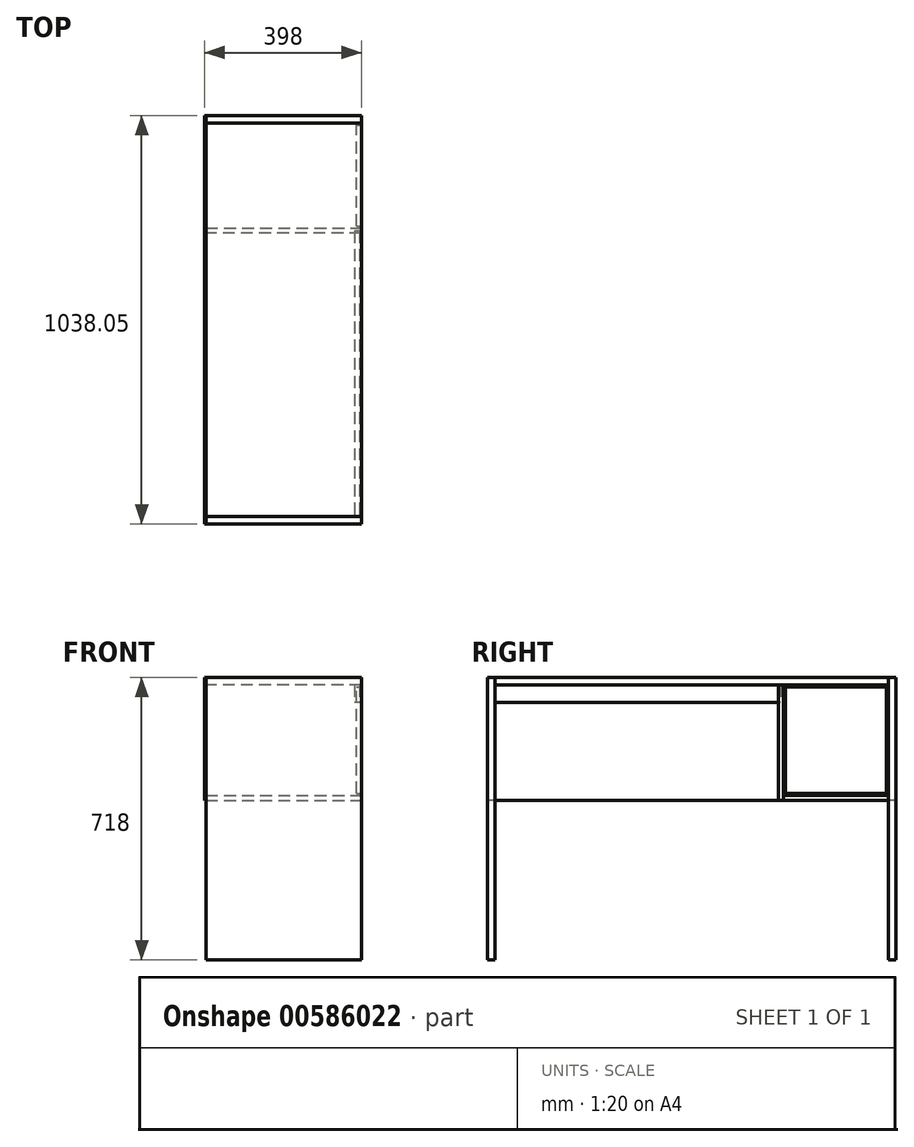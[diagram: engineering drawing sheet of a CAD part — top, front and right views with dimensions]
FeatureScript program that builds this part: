
annotation { "Feature Type Name" : "Feature", "Feature Type Description" : "" }
export const myFeature = defineFeature(function(context is Context, id is Id, definition is map)
    precondition{}
    {
        {
            var Q0;
            Q0=qCreatedBy(makeId("Front.planeOp"),FACE);
            var sketch = newSketch(context, id + "F0", { "sketchPlane" : qUnion([Q0])});
            skLineSegment(sketch, "E0.bottom", {"start": v(197.5, 359) * mm, "end": v(-197.5, 359) * mm});
            skLineSegment(sketch, "E0.top", {"start": v(197.5, -359) * mm, "end": v(-197.5, -359) * mm});
            skLineSegment(sketch, "E0.left", {"start": v(197.5, 359) * mm, "end": v(197.5, -359) * mm});
            skLineSegment(sketch, "E0.right", {"start": v(-197.5, 359) * mm, "end": v(-197.5, -359) * mm});
            skPoint(sketch, "E0.middle", {"position": v(0, 0) * mm});
            skSolve(sketch);
        }
        {
            var Q0;
            Q0 = qSketchRegion(id + "F0", true);
            extrude(context, id + "F1", {"entities" : qUnion([Q0]), "depth" : 19.05 * mm, "offsetDistance" : 25.4 * mm});
        }
        {
            var Q0;
            Q0=makeQuery(id+"F1.opExtrude","SWEPT_BODY",BODY,{"disambiguationData":[OSD([sQuery(id+"F0.wireOp",EDGE,"E0.bottom"),sQuery(id+"F0.wireOp",EDGE,"E0.top"),sQuery(id+"F0.wireOp",EDGE,"E0.left"),sQuery(id+"F0.wireOp",EDGE,"E0.right")])]});
            transform(context, id + "F2", {"entities" : qUnion([Q0]), "transformType" : TransformType.TRANSLATION_3D, "dx" : 0 * mm, "dy" : 1019 * mm, "dz" : 0 * mm, "makeCopy" : true});
        }
        {
            var Q0;
            Q0=makeQuery(id+"F1.opExtrude","SWEPT_FACE",FACE,{"disambiguationData":[OSD([sQuery(id+"F0.wireOp",EDGE,"E0.bottom")])]});
            var sketch = newSketch(context, id + "F3", { "sketchPlane" : qUnion([Q0])});
            skLineSegment(sketch, "E1.bottom", {"start": v(197.5, 0) * mm, "end": v(-197.5, 0) * mm});
            skLineSegment(sketch, "E1.top", {"start": v(197.5, 1000) * mm, "end": v(-197.5, 1000) * mm});
            skLineSegment(sketch, "E1.left", {"start": v(197.5, 0) * mm, "end": v(197.5, 1000) * mm});
            skLineSegment(sketch, "E1.right", {"start": v(-197.5, 0) * mm, "end": v(-197.5, 1000) * mm});
            skSolve(sketch);
        }
        {
            var Q0;
            Q0 = qSketchRegion(id + "F3", true);
            extrude(context, id + "F4", {"entities" : qUnion([Q0]), "oppositeDirection" : true, "depth" : 19 * mm, "offsetDistance" : 25 * mm});
        }
        {
            var Q0;
            Q0=makeQuery(id+"F4.opExtrude","CAP_FACE",FACE,{"disambiguationData":[OSD([sQuery(id+"F3.wireOp",EDGE,"E1.bottom"),sQuery(id+"F3.wireOp",EDGE,"E1.top"),sQuery(id+"F3.wireOp",EDGE,"E1.left"),sQuery(id+"F3.wireOp",EDGE,"E1.right")])],"isStart":false});
            var sketch = newSketch(context, id + "F5", { "sketchPlane" : qUnion([Q0])});
            skLineSegment(sketch, "E2.bottom", {"start": v(197.5, -720.25) * mm, "end": v(-197.5, -720.25) * mm});
            skLineSegment(sketch, "E2.top", {"start": v(197.5, -732.95) * mm, "end": v(-197.5, -732.95) * mm});
            skLineSegment(sketch, "E2.left", {"start": v(197.5, -720.25) * mm, "end": v(197.5, -732.95) * mm});
            skLineSegment(sketch, "E2.right", {"start": v(-197.5, -720.25) * mm, "end": v(-197.5, -732.95) * mm});
            skSolve(sketch);
        }
        {
            var Q0;
            Q0=makeQuery(id+"F5.imprint","IMPRINT",FACE,{"disambiguationData":[TD([[makeQuery(id+"F5.imprint","IMPRINT",EDGE,{"derivedFrom":sQuery(id+"F5.wireOp",EDGE,"E2.bottom")}),1.0]])]});
            extrude(context, id + "F6", {"entities" : qUnion([Q0]), "depth" : 293 * mm, "offsetDistance" : 25 * mm});
        }
        {
            var Q0;
            Q0=makeQuery(id+"F6.opExtrude","SWEPT_FACE",FACE,{"disambiguationData":[OSD([sQuery(id+"F5.wireOp",EDGE,"E2.left")])]});
            var sketch = newSketch(context, id + "F7", { "sketchPlane" : qUnion([Q0])});
            skLineSegment(sketch, "E3.bottom", {"start": v(732.95, 47) * mm, "end": v(999.95, 47) * mm});
            skLineSegment(sketch, "E3.top", {"start": v(732.95, 59.7) * mm, "end": v(999.95, 59.7) * mm});
            skLineSegment(sketch, "E3.left", {"start": v(732.95, 47) * mm, "end": v(732.95, 59.7) * mm});
            skLineSegment(sketch, "E3.right", {"start": v(999.95, 47) * mm, "end": v(999.95, 59.7) * mm});
            skSolve(sketch);
        }
        {
            var Q0;
            Q0 = qSketchRegion(id + "F7", true);
            extrude(context, id + "F8", {"entities" : qUnion([Q0]), "oppositeDirection" : true, "depth" : 395 * mm, "offsetDistance" : 25 * mm});
        }
        {
            var Q0;
            Q0=makeQuery(id+"F2.opPattern","COPY",FACE,{"derivedFrom":makeQuery(id+"F1.opExtrude","SWEPT_FACE",FACE,{"disambiguationData":[OSD([sQuery(id+"F0.wireOp",EDGE,"E0.right")])]}),"instanceName":"1"});
            var sketch = newSketch(context, id + "F9", { "sketchPlane" : qUnion([Q0])});
            skLineSegment(sketch, "E4.bottom", {"start": v(-1019, 47) * mm, "end": v(19, 47) * mm});
            skLineSegment(sketch, "E4.top", {"start": v(-1019, 359) * mm, "end": v(19, 359) * mm});
            skLineSegment(sketch, "E4.left", {"start": v(-1019, 47) * mm, "end": v(-1019, 366) * mm});
            skLineSegment(sketch, "E4.right", {"start": v(19, 47) * mm, "end": v(19, 366) * mm});
            skSolve(sketch);
        }
        {
            var Q0;
            Q0 = qSketchRegion(id + "F9", true);
            extrude(context, id + "F10", {"entities" : qUnion([Q0]), "depth" : 3 * mm, "offsetDistance" : 25 * mm});
        }
        {
            var Q0;
            Q0=makeQuery(id+"F8.opExtrude","CAP_FACE",FACE,{"disambiguationData":[OSD([sQuery(id+"F7.wireOp",EDGE,"E3.bottom"),sQuery(id+"F7.wireOp",EDGE,"E3.top"),sQuery(id+"F7.wireOp",EDGE,"E3.left"),sQuery(id+"F7.wireOp",EDGE,"E3.right")])],"isStart":true});
            var sketch = newSketch(context, id + "F11", { "sketchPlane" : qUnion([Q0])});
            skLineSegment(sketch, "E5.bottom", {"start": v(738.45, 64.7) * mm, "end": v(994.45, 64.7) * mm});
            skLineSegment(sketch, "E5.top", {"start": v(738.45, 334.7) * mm, "end": v(994.45, 334.7) * mm});
            skLineSegment(sketch, "E5.left", {"start": v(738.45, 64.7) * mm, "end": v(738.45, 334.7) * mm});
            skLineSegment(sketch, "E5.right", {"start": v(994.45, 64.7) * mm, "end": v(994.45, 334.7) * mm});
            skSolve(sketch);
        }
        {
            var Q0;
            Q0=makeQuery(id+"F11.imprint","IMPRINT",FACE,{"disambiguationData":[TD([[makeQuery(id+"F11.imprint","IMPRINT",EDGE,{"derivedFrom":sQuery(id+"F11.wireOp",EDGE,"E5.bottom")}),1.0]])]});
            extrude(context, id + "F12", {"entities" : qUnion([Q0]), "oppositeDirection" : true, "depth" : 12.7 * mm, "offsetDistance" : 25 * mm});
        }
        {
            var Q0;
            Q0=makeQuery(id+"F0.imprint","IMPRINT",FACE,{"disambiguationData":[TD([[makeQuery(id+"F0.imprint","IMPRINT",EDGE,{"derivedFrom":sQuery(id+"F0.wireOp",EDGE,"E0.bottom")}),1.0]])]});
            var sketch = newSketch(context, id + "F13", { "sketchPlane" : qUnion([Q0])});
            skLineSegment(sketch, "E6.bottom", {"start": v(192.5, 340) * mm, "end": v(179.8, 340) * mm});
            skLineSegment(sketch, "E6.top", {"start": v(192.5, 296) * mm, "end": v(179.8, 296) * mm});
            skLineSegment(sketch, "E6.left", {"start": v(192.5, 340) * mm, "end": v(192.5, 296) * mm});
            skLineSegment(sketch, "E6.right", {"start": v(179.8, 340) * mm, "end": v(179.8, 296) * mm});
            skSolve(sketch);
        }
        {
            var Q0;
            Q0 = qSketchRegion(id + "F13", true);
            extrude(context, id + "F14", {"entities" : qUnion([Q0]), "oppositeDirection" : true, "depth" : 725 * mm, "offsetDistance" : 25 * mm});
        }
    });
